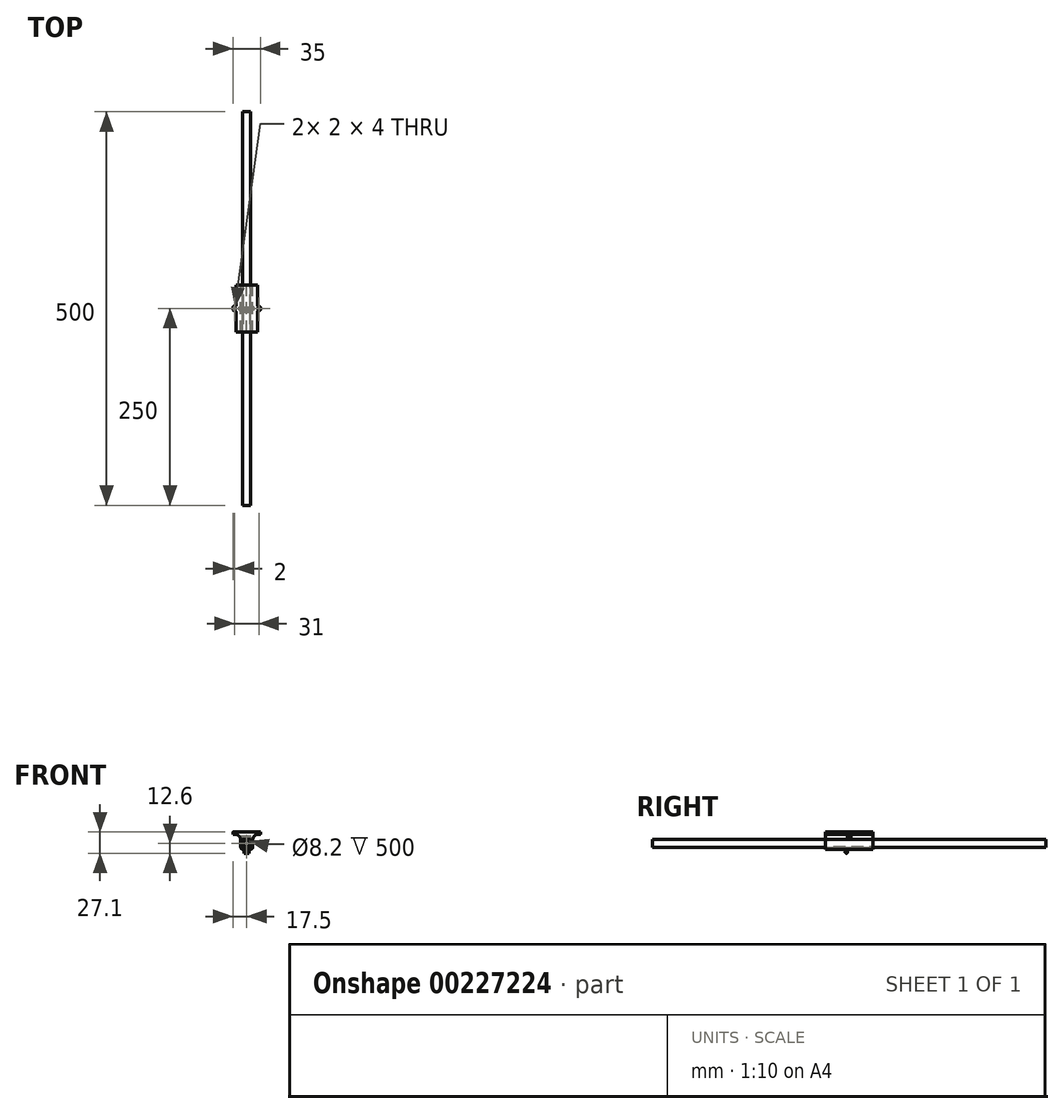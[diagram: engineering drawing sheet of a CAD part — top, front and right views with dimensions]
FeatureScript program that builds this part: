
annotation { "Feature Type Name" : "Feature", "Feature Type Description" : "" }
export const myFeature = defineFeature(function(context is Context, id is Id, definition is map)
    precondition{}
    {
        {
            var Q0;
            Q0=qCreatedBy(makeId("Front.planeOp"),FACE);
            var sketch = newSketch(context, id + "F0", { "sketchPlane" : qUnion([Q0])});
            skLineSegment(sketch, "E0.bottom", {"start": v(5, -5) * mm, "end": v(-5, -5) * mm});
            skLineSegment(sketch, "E0.top", {"start": v(5, 5) * mm, "end": v(-5, 5) * mm});
            skLineSegment(sketch, "E0.left", {"start": v(5, -5) * mm, "end": v(5, 5) * mm});
            skLineSegment(sketch, "E0.right", {"start": v(-5, -5) * mm, "end": v(-5, 5) * mm});
            skPoint(sketch, "E0.middle", {"position": v(0, 0) * mm});
            skCircle(sketch, "E1", {"center": v(0, 0) * mm, "radius": 4.1 * mm});
            skSolve(sketch);
        }
        {
            var Q0;
            Q0=qSketchRegion(id+"F0",true);
            extrude(context, id + "F1", {"entities" : qUnion([Q0]), "depth" : 500 * mm});
        }
        {
            var Q0;
            Q0=qCreatedBy(makeId("Front.planeOp"),FACE);
            cPlane(context, id + "F2", {"entities" : qUnion([Q0]), "cplaneType" : CPlaneType.OFFSET, "offset" : 250 * mm, "width" : 150 * mm, "height" : 150 * mm});
        }
        {
            var Q0;
            Q0=qCreatedBy(id+"F2.planeOp",FACE);
            var sketch = newSketch(context, id + "F3", { "sketchPlane" : qUnion([Q0])});
            skLineSegment(sketch, "E2.bottom", {"start": v(-5, 7.5) * mm, "end": v(5, 7.5) * mm});
            skLineSegment(sketch, "E2.top", {"start": v(-5, -7.5) * mm, "end": v(5, -7.5) * mm});
            skLineSegment(sketch, "E2.left", {"start": v(-7.5, 5) * mm, "end": v(-7.5, -5) * mm});
            skLineSegment(sketch, "E2.right", {"start": v(7.5, 5) * mm, "end": v(7.5, -5) * mm});
            skPoint(sketch, "E2.middle", {"position": v(0, 0) * mm});
            skLineSegment(sketch, "E3.0", {"start": v(5, 5) * mm, "end": v(-5, 5) * mm});
            skLineSegment(sketch, "E4.0", {"start": v(5, -5) * mm, "end": v(5, 5) * mm});
            skLineSegment(sketch, "E5.0", {"start": v(5, -5) * mm, "end": v(-5, -5) * mm});
            skLineSegment(sketch, "E6.0", {"start": v(-5, -5) * mm, "end": v(-5, 5) * mm});
            skLineSegment(sketch, "E7.bottom", {"start": v(-5.2, 5.2) * mm, "end": v(5.2, 5.2) * mm});
            skLineSegment(sketch, "E7.top", {"start": v(-5.2, -5.2) * mm, "end": v(5.2, -5.2) * mm});
            skLineSegment(sketch, "E7.left", {"start": v(-5.2, 5.2) * mm, "end": v(-5.2, -5.2) * mm});
            skLineSegment(sketch, "E7.right", {"start": v(5.2, 5.2) * mm, "end": v(5.2, -5.2) * mm});
            skPoint(sketch, "E8.visualSharp", {"position": v(-7.5, 7.5) * mm});
            skArc(sketch, "E8.filletArc", {"start": v(-5, 7.5) * mm, "mid": v(-6.77, 6.77) * mm, "end": v(-7.5, 5) * mm});
            skPoint(sketch, "E9.visualSharp", {"position": v(7.5, 7.5) * mm});
            skArc(sketch, "E9.filletArc", {"start": v(7.5, 5) * mm, "mid": v(6.77, 6.77) * mm, "end": v(5, 7.5) * mm});
            skPoint(sketch, "E10.visualSharp", {"position": v(-7.5, -7.5) * mm});
            skArc(sketch, "E10.filletArc", {"start": v(-7.5, -5) * mm, "mid": v(-6.77, -6.77) * mm, "end": v(-5, -7.5) * mm});
            skPoint(sketch, "E11.visualSharp", {"position": v(7.5, -7.5) * mm});
            skArc(sketch, "E11.filletArc", {"start": v(5, -7.5) * mm, "mid": v(6.77, -6.77) * mm, "end": v(7.5, -5) * mm});
            skLineSegment(sketch, "E12.bottom", {"start": v(-3.15, -7.5) * mm, "end": v(3.15, -7.5) * mm});
            skLineSegment(sketch, "E12.top", {"start": v(-3.15, -14.5) * mm, "end": v(3.15, -14.5) * mm});
            skLineSegment(sketch, "E12.left", {"start": v(-3.15, -7.5) * mm, "end": v(-3.15, -14.5) * mm});
            skLineSegment(sketch, "E12.right", {"start": v(3.15, -7.5) * mm, "end": v(3.15, -14.5) * mm});
            skLineSegment(sketch, "E13", {"start": v(-3.15, -11) * mm, "end": v(0, -11) * mm, "construction": true});
            skLineSegment(sketch, "E14", {"start": v(0, -11) * mm, "end": v(3.15, -11) * mm, "construction": true});
            skLineSegment(sketch, "E15.bottom", {"start": v(-0.15, -7.5) * mm, "end": v(0.15, -7.5) * mm});
            skLineSegment(sketch, "E15.top", {"start": v(-0.15, -14.5) * mm, "end": v(0.15, -14.5) * mm});
            skLineSegment(sketch, "E15.left", {"start": v(-0.15, -7.5) * mm, "end": v(-0.15, -14.5) * mm});
            skLineSegment(sketch, "E15.right", {"start": v(0.15, -7.5) * mm, "end": v(0.15, -14.5) * mm});
            skPoint(sketch, "E15.middle", {"position": v(0, -11) * mm});
            skLineSegment(sketch, "E16", {"start": v(-0.15, -7.5) * mm, "end": v(-0.15, -5.2) * mm});
            skLineSegment(sketch, "E17", {"start": v(0.15, -7.5) * mm, "end": v(0.15, -5.2) * mm});
            skLineSegment(sketch, "E18.bottom", {"start": v(-13.5, 14.5) * mm, "end": v(13.5, 14.5) * mm});
            skLineSegment(sketch, "E18.top", {"start": v(-13.5, 11.5) * mm, "end": v(13.5, 11.5) * mm});
            skLineSegment(sketch, "E18.left", {"start": v(-13.5, 14.5) * mm, "end": v(-13.5, 11.5) * mm});
            skLineSegment(sketch, "E18.right", {"start": v(13.5, 14.5) * mm, "end": v(13.5, 11.5) * mm});
            skPoint(sketch, "E18.middle", {"position": v(0, 13) * mm});
            skFitSpline(sketch, "E19", {"points": [v(-13.5, 11.5) * mm, v(-7.5, 5) * mm], "startDerivative": vector(13.52, -2.45) * mm, "endDerivative": vector(2.59, -4.91) * mm});
            skFitSpline(sketch, "E20.MirrorCS", {"points": [v(13.5, 11.5) * mm, v(7.5, 5) * mm], "startDerivative": vector(-13.52, -2.45) * mm, "endDerivative": vector(-2.59, -4.91) * mm});
            skSolve(sketch);
        }
        {
            var Q0;
            Q0=makeQuery(id+"F3.imprint","IMPRINT",FACE,{"disambiguationData":[TD([[makeQuery(id+"F3.imprint","IMPRINT",EDGE,{"derivedFrom":sQuery(id+"F3.wireOp",EDGE,"E2.bottom")}),-1.0]])]});
            var Q1;
            Q1=makeQuery(id+"F3.imprint","IMPRINT",FACE,{"disambiguationData":[TD([[makeQuery(id+"F3.imprint","IMPRINT",EDGE,{"derivedFrom":sQuery(id+"F3.wireOp",EDGE,"E18.bottom")}),-1.0]])]});
            var Q2;
            Q2=makeQuery(id+"F3.imprint","IMPRINT",FACE,{"disambiguationData":[TD([[makeQuery(id+"F3.imprint","IMPRINT",EDGE,{"derivedFrom":sQuery(id+"F3.wireOp",EDGE,"E2.bottom")}),1.0]])]});
            extrude(context, id + "F4", {"entities" : qUnion([Q0, Q1, Q2]), "endBound" : BoundingType.SYMMETRIC, "depth" : 60 * mm});
        }
        {
            var Q0;
            {var subQ0=sQuery(id+"F3.wireOp",EDGE,"E12.left");Q0=makeQuery(id+"F3.imprint","IMPRINT",FACE,{"disambiguationData":[TD([[makeQuery(id+"F3.imprint","IMPRINT",EDGE,{"derivedFrom":subQ0}),1.0]])]});}
            var Q1;
            {var subQ0=sQuery(id+"F3.wireOp",EDGE,"E12.right");Q1=makeQuery(id+"F3.imprint","IMPRINT",FACE,{"disambiguationData":[TD([[makeQuery(id+"F3.imprint","IMPRINT",EDGE,{"derivedFrom":subQ0}),-1.0]])]});}
            extrude(context, id + "F5", {"entities" : qUnion([Q0, Q1]), "operationType" : NewBodyOperationType.ADD, "endBound" : BoundingType.SYMMETRIC, "depth" : 14 * mm});
        }
        {
            var Q0;
            Q0=makeQuery(id+"F5.opExtrude","SWEPT_FACE",FACE,{"disambiguationData":[OSD([sQuery(id+"F3.wireOp",EDGE,"E12.left")])]});
            var sketch = newSketch(context, id + "F6", { "sketchPlane" : qUnion([Q0])});
            skLineSegment(sketch, "E21", {"start": v(250, -7.5) * mm, "end": v(250, -14.5) * mm, "construction": true});
            skLineSegment(sketch, "E22", {"start": v(250, -11) * mm, "end": v(243, -11) * mm, "construction": true});
            skCircle(sketch, "E23", {"center": v(246.5, -11) * mm, "radius": 1.6 * mm});
            skCircle(sketch, "E24.MirrorC", {"center": v(253.5, -11) * mm, "radius": 1.6 * mm});
            skSolve(sketch);
        }
        {
            var Q0;
            Q0=makeQuery(id+"F6.imprint","IMPRINT",FACE,{"disambiguationData":[TD([[makeQuery(id+"F6.imprint","IMPRINT",EDGE,{"derivedFrom":sQuery(id+"F6.wireOp",EDGE,"E23")}),1.0]])]});
            var Q1;
            Q1=makeQuery(id+"F6.imprint","IMPRINT",FACE,{"disambiguationData":[TD([[makeQuery(id+"F6.imprint","IMPRINT",EDGE,{"derivedFrom":sQuery(id+"F6.wireOp",EDGE,"E24.MirrorC")}),-1.0]])]});
            extrude(context, id + "F7", {"entities" : qUnion([Q0, Q1]), "operationType" : NewBodyOperationType.REMOVE, "oppositeDirection" : true, "depth" : 25 * mm});
        }
        {
            var Q0;
            Q0=makeQuery(id+"F4.opExtrude","SWEPT_FACE",FACE,{"disambiguationData":[OSD([sQuery(id+"F3.wireOp",EDGE,"E18.bottom")])]});
            var sketch = newSketch(context, id + "F8", { "sketchPlane" : qUnion([Q0])});
            skLineSegment(sketch, "E25.bottom", {"start": v(-17.5, -247) * mm, "end": v(-9.5, -247) * mm});
            skLineSegment(sketch, "E25.top", {"start": v(-17.5, -253) * mm, "end": v(-9.5, -253) * mm});
            skLineSegment(sketch, "E25.left", {"start": v(-17.5, -247) * mm, "end": v(-17.5, -253) * mm});
            skLineSegment(sketch, "E25.right", {"start": v(-9.5, -247) * mm, "end": v(-9.5, -253) * mm, "construction": true});
            skPoint(sketch, "E25.middle", {"position": v(-13.5, -250) * mm});
            skLineSegment(sketch, "E26", {"start": v(-13.5, -250) * mm, "end": v(-17.5, -250) * mm, "construction": true});
            skLineSegment(sketch, "E27", {"start": v(-13.5, -253) * mm, "end": v(-13.5, -247) * mm});
            skLineSegment(sketch, "E28.bottom", {"start": v(-16.5, -248) * mm, "end": v(-14.5, -248) * mm});
            skLineSegment(sketch, "E28.top", {"start": v(-16.5, -252) * mm, "end": v(-14.5, -252) * mm});
            skLineSegment(sketch, "E28.left", {"start": v(-16.5, -248) * mm, "end": v(-16.5, -252) * mm});
            skLineSegment(sketch, "E28.right", {"start": v(-14.5, -248) * mm, "end": v(-14.5, -252) * mm});
            skPoint(sketch, "E28.middle", {"position": v(-15.5, -250) * mm});
            skLineSegment(sketch, "E29.MirrorCS", {"start": v(17.5, -247) * mm, "end": v(17.5, -253) * mm});
            skLineSegment(sketch, "E30.MirrorCS", {"start": v(17.5, -253) * mm, "end": v(9.5, -253) * mm});
            skLineSegment(sketch, "E31.MirrorCS", {"start": v(13.5, -253) * mm, "end": v(13.5, -247) * mm});
            skLineSegment(sketch, "E32.MirrorCS", {"start": v(17.5, -247) * mm, "end": v(9.5, -247) * mm});
            skLineSegment(sketch, "E33.MirrorCS", {"start": v(16.5, -248) * mm, "end": v(14.5, -248) * mm});
            skLineSegment(sketch, "E34.MirrorCS", {"start": v(16.5, -248) * mm, "end": v(16.5, -252) * mm});
            skLineSegment(sketch, "E35.MirrorCS", {"start": v(16.5, -252) * mm, "end": v(14.5, -252) * mm});
            skLineSegment(sketch, "E36.MirrorCS", {"start": v(14.5, -248) * mm, "end": v(14.5, -252) * mm});
            skSolve(sketch);
        }
        {
            var Q0;
            {var subQ1=sQuery(id+"F8.wireOp",EDGE,"E29.MirrorCS");Q0=makeQuery(id+"F8.imprint","IMPRINT",FACE,{"disambiguationData":[TD([[makeQuery(id+"F8.imprint","IMPRINT",EDGE,{"derivedFrom":subQ1}),-1.0]])]});}
            var Q1;
            {var subQ1=sQuery(id+"F8.wireOp",EDGE,"E25.left");Q1=makeQuery(id+"F8.imprint","IMPRINT",FACE,{"disambiguationData":[TD([[makeQuery(id+"F8.imprint","IMPRINT",EDGE,{"derivedFrom":subQ1}),1.0]])]});}
            extrude(context, id + "F9", {"entities" : qUnion([Q0, Q1]), "operationType" : NewBodyOperationType.ADD, "oppositeDirection" : true, "depth" : 3 * mm});
        }
        {
            var Q0;
            Q0=makeQuery(id+"F9.opExtrude","SWEPT_EDGE",EDGE,{"disambiguationData":[OSD([sQuery(id+"F8.wireOp",EDGE,"E25.bottom"),sQuery(id+"F8.wireOp",EDGE,"E25.left")])]});
            var Q1;
            Q1=makeQuery(id+"F9.opExtrude","SWEPT_EDGE",EDGE,{"disambiguationData":[OSD([sQuery(id+"F3.wireOp",EDGE,"E18.bottom"),sQuery(id+"F3.wireOp",EDGE,"E18.left"),sQuery(id+"F8.wireOp",EDGE,"E25.bottom"),sQuery(id+"F8.wireOp",EDGE,"E27")])]});
            var Q2;
            Q2=makeQuery(id+"F9.opExtrude","SWEPT_EDGE",EDGE,{"disambiguationData":[OSD([sQuery(id+"F8.wireOp",EDGE,"E25.top"),sQuery(id+"F8.wireOp",EDGE,"E25.left")])]});
            var Q3;
            Q3=makeQuery(id+"F9.opExtrude","SWEPT_EDGE",EDGE,{"disambiguationData":[OSD([sQuery(id+"F3.wireOp",EDGE,"E18.bottom"),sQuery(id+"F3.wireOp",EDGE,"E18.left"),sQuery(id+"F8.wireOp",EDGE,"E25.top"),sQuery(id+"F8.wireOp",EDGE,"E27")])]});
            var Q4;
            Q4=makeQuery(id+"F9.opExtrude","SWEPT_EDGE",EDGE,{"disambiguationData":[OSD([sQuery(id+"F8.wireOp",EDGE,"E29.MirrorCS"),sQuery(id+"F8.wireOp",EDGE,"E32.MirrorCS")])]});
            var Q5;
            Q5=makeQuery(id+"F9.opExtrude","SWEPT_EDGE",EDGE,{"disambiguationData":[OSD([sQuery(id+"F3.wireOp",EDGE,"E18.bottom"),sQuery(id+"F3.wireOp",EDGE,"E18.right"),sQuery(id+"F8.wireOp",EDGE,"E31.MirrorCS"),sQuery(id+"F8.wireOp",EDGE,"E32.MirrorCS")])]});
            var Q6;
            Q6=makeQuery(id+"F9.opExtrude","SWEPT_EDGE",EDGE,{"disambiguationData":[OSD([sQuery(id+"F3.wireOp",EDGE,"E18.bottom"),sQuery(id+"F3.wireOp",EDGE,"E18.right"),sQuery(id+"F8.wireOp",EDGE,"E30.MirrorCS"),sQuery(id+"F8.wireOp",EDGE,"E31.MirrorCS")])]});
            var Q7;
            Q7=makeQuery(id+"F9.opExtrude","SWEPT_EDGE",EDGE,{"disambiguationData":[OSD([sQuery(id+"F8.wireOp",EDGE,"E29.MirrorCS"),sQuery(id+"F8.wireOp",EDGE,"E30.MirrorCS")])]});
            fillet(context, id + "F10", {"entities" : qUnion([Q0, Q1, Q2, Q3, Q4, Q5, Q6, Q7]), "radius" : 2 * mm, "tangentPropagation" : true, "allowEdgeOverflow" : false});
        }
        {
            var Q0;
            {var subQ8=sQuery(id+"F8.wireOp",EDGE,"E30.MirrorCS");var subQ10=sQuery(id+"F3.wireOp",EDGE,"E18.right");Q0=makeQuery(id+"F9.boolean.opBoolean","SPLIT",FACE,{"disambiguationData":[TD([makeQuery(id+"F9.opExtrude","SWEPT_FACE",FACE,{"disambiguationData":[OSD([subQ8])]})])],"derivedFrom":makeQuery(id+"F4.opExtrude","SWEPT_FACE",FACE,{"disambiguationData":[OSD([subQ10])]})});}
            var sketch = newSketch(context, id + "F11", { "sketchPlane" : qUnion([Q0])});
            skFitSpline(sketch, "E37.0.0", {"points": [v(-220, 5) * mm, v(-220, 6.64) * mm, v(-220, 10.68) * mm, v(-220, 11.5) * mm], "construction": true});
            skLineSegment(sketch, "E37.0.1", {"start": v(-220, 11.5) * mm, "end": v(-245, 11.5) * mm, "construction": true});
            skLineSegment(sketch, "E37.0.2", {"start": v(-245, 11.5) * mm, "end": v(-255, 11.5) * mm, "construction": true});
            skLineSegment(sketch, "E37.0.3", {"start": v(-255, 11.5) * mm, "end": v(-280, 11.5) * mm, "construction": true});
            skFitSpline(sketch, "E37.0.4", {"points": [v(-280, 11.5) * mm, v(-280, 10.68) * mm, v(-280, 6.64) * mm, v(-280, 5) * mm], "construction": true});
            skLineSegment(sketch, "E37.0.5", {"start": v(-280, 5) * mm, "end": v(-220, 5) * mm, "construction": true});
            skLineSegment(sketch, "E38", {"start": v(-250, 11.5) * mm, "end": v(-250, 5) * mm, "construction": true});
            skLineSegment(sketch, "E39.bottom", {"start": v(-252, 9.25) * mm, "end": v(-248, 9.25) * mm});
            skLineSegment(sketch, "E39.top", {"start": v(-252, 7.25) * mm, "end": v(-248, 7.25) * mm});
            skLineSegment(sketch, "E39.left", {"start": v(-252, 9.25) * mm, "end": v(-252, 7.25) * mm});
            skLineSegment(sketch, "E39.right", {"start": v(-248, 9.25) * mm, "end": v(-248, 7.25) * mm});
            skPoint(sketch, "E39.middle", {"position": v(-250, 8.25) * mm});
            skSolve(sketch);
        }
        {
            var Q0;
            Q0=makeQuery(id+"F11.imprint","IMPRINT",FACE,{"disambiguationData":[TD([[makeQuery(id+"F11.imprint","IMPRINT",EDGE,{"derivedFrom":sQuery(id+"F11.wireOp",EDGE,"E39.bottom")}),-1.0]])]});
            extrude(context, id + "F12", {"entities" : qUnion([Q0]), "operationType" : NewBodyOperationType.REMOVE, "oppositeDirection" : true, "depth" : 25 * mm});
        }
    });
